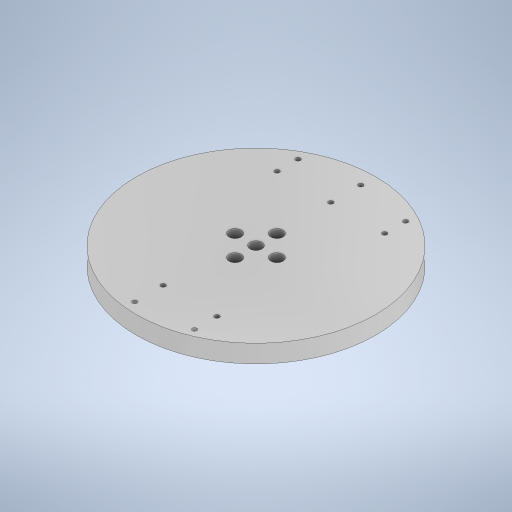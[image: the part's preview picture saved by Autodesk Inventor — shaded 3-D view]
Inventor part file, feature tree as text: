
AUTODESK INVENTOR PART (.ipt)
format: ipt  version: 2024.2 (Build 282272000, 272)  size: 296,960 bytes
history: native  units: in
note: dims shown in document units (in); Inventor stores cm internally (conversion verified against a paired STEP export)
features: reference x17, sketch x7, extrude x5, other x5, hole x2, projected_geometry x1
ambient origin geometry x8: Origin, YZ Plane, XZ Plane, XY Plane, X Axis, Y Axis, Z Axis, Center Point
bodies: Solid1 (feature_tree)
feature tree (37):
  extrude  "Extrusion1"  Depth=0.2362in TaperAngle=0.0deg
  extrude  "Extrusion2"  Depth=0.0787in
  hole  "Hole1"  [1 undecoded]
  extrude  "Extrusion3"  Depth=0.0591in TaperAngle=0.0deg
  extrude  "Extrusion4"  Depth=0.1181in
  extrude  "Extrusion5"  [1 undecoded]
  hole  "Hole2"  [1 undecoded]
  sketch  "Sketch1"  dims[d0=3.1496in d1=0.2362in d2=0.0in]
  sketch  "Sketch2"  dims[d3=0.0563in d4=0.0in]
  reference  "Reference1"
  reference  "Reference2"
  sketch  "Sketch3"  dims[d5=0.0827in d6=0.2362in d7=0.119in d8=0.0787in d9=0.5635in d10=0.315in d11=0.8108in d12=0.1614in]
  reference  "Reference3"
  reference  "Reference4"
  reference  "Reference5"
  reference  "Reference6"
  sketch  "Sketch4"  dims[d13=0.1181in d14=0.0in d15=0.0in d16=0.0in]
  projected_geometry  "Projected Loop1"
  sketch  "Sketch5"  dims[d17=0.2362in d18=0.0591in d19=0.0in]
  reference  "Reference7"
  sketch  "Sketch6"  dims[d20=0.0617in d21=0.1181in d22=0.1575in d23=0.0787in d24=90.0deg d25=0.1181in d26=0.0in d27=0.1575in]
  sketch  "Sketch7"
  reference  "Reference8"
  reference  "Reference9"
  reference  "Reference10"
  reference  "Reference11"
  reference  "Reference12"
  reference  "Reference13"
  reference  "Reference14"
  reference  "Reference15"
  reference  "Reference16"
  reference  "Reference17"
  other  "2_Arm.iam"
  other  "axis_1_top_frame:1"
  other  "Top Horn:1"
  other  "axis_2_bottom_L_frame(top):1"
  other  "axis_2_bottom_L_frame(bottom):1"
note: 3 required parameter values undecoded (feature->parameter linkage not recoverable at this tier; creation-order binding heuristic only, values carry confidence <= 0.55)
